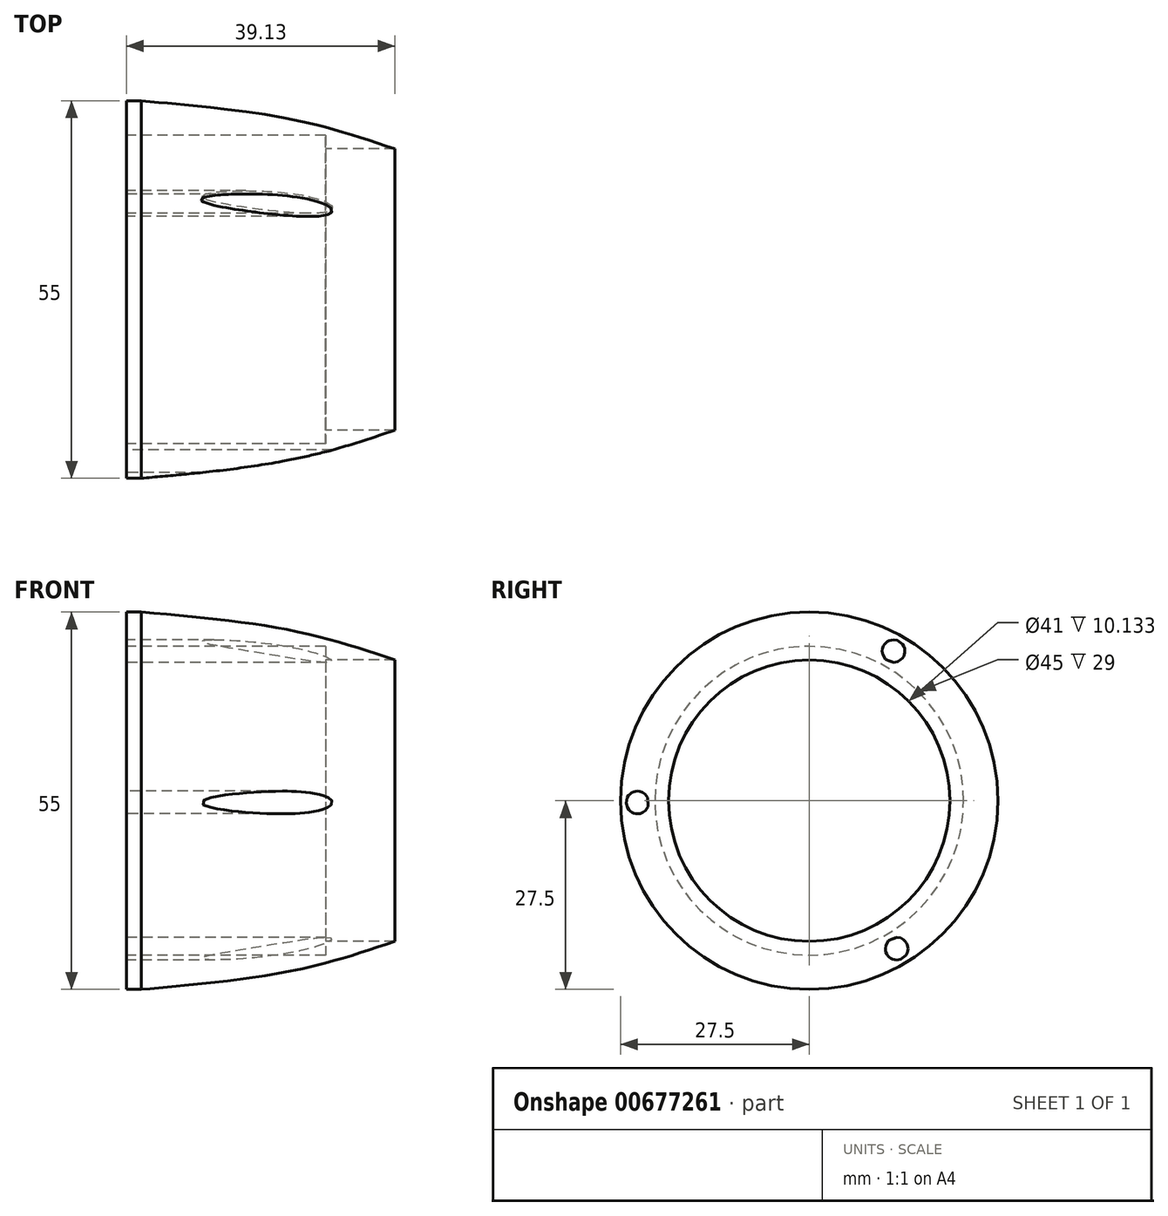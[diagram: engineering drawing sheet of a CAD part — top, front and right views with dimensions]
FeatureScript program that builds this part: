
annotation { "Feature Type Name" : "Feature", "Feature Type Description" : "" }
export const myFeature = defineFeature(function(context is Context, id is Id, definition is map)
    precondition{}
    {
        {
            var Q0;
            Q0=qCreatedBy(makeId("Front.planeOp"),FACE);
            var sketch = newSketch(context, id + "F0", { "sketchPlane" : qUnion([Q0])});
            skLineSegment(sketch, "E0", {"start": v(-29.3, 0) * mm, "end": v(30.63, 0) * mm, "construction": true});
            skLineSegment(sketch, "E1.top", {"start": v(-17.31, 22.5) * mm, "end": v(11.69, 22.5) * mm});
            skLineSegment(sketch, "E1.left", {"start": v(-17.31, 27.5) * mm, "end": v(-17.31, 22.5) * mm});
            skPoint(sketch, "E2", {"position": v(21.82, 20.5) * mm});
            skLineSegment(sketch, "E3", {"start": v(21.82, 20.5) * mm, "end": v(11.69, 20.5) * mm});
            skLineSegment(sketch, "E4", {"start": v(11.69, 20.5) * mm, "end": v(11.69, 22.5) * mm});
            skLineSegment(sketch, "E5", {"start": v(-17.31, 27.5) * mm, "end": v(-15.14, 27.5) * mm});
            skFitSpline(sketch, "E6", {"points": [v(-15.14, 27.5) * mm, v(6.94, 24.78) * mm, v(21.82, 20.5) * mm], "startDerivative": vector(42.6, -3.8) * mm, "endDerivative": vector(30.96, -10.4) * mm});
            skSolve(sketch);
        }
        {
            var Q0;
            Q0=makeQuery(id+"F0.imprint","IMPRINT",FACE,{"disambiguationData":[TD([[makeQuery(id+"F0.imprint","IMPRINT",EDGE,{"derivedFrom":sQuery(id+"F0.wireOp",EDGE,"E1.top")}),1.0]])]});
            var Q1;
            Q1=sQuery(id+"F0.wireOp",EDGE,"E0");
            revolve(context, id + "F1", {"entities" : qUnion([Q0]), "axis" : qUnion([Q1]), "revolveType" : RevolveType.FULL});
        }
        {
            var Q0;
            Q0=makeQuery(id+"F1.opRevolve","SWEPT_FACE",FACE,{"disambiguationData":[OSD([sQuery(id+"F0.wireOp",EDGE,"E1.left")])]});
            var sketch = newSketch(context, id + "F2", { "sketchPlane" : qUnion([Q0])});
            skCircle(sketch, "E7", {"center": v(-12.3, 21.8) * mm, "radius": 1.65 * mm});
            skCircle(sketch, "E8.1.0", {"center": v(-12.74, -21.55) * mm, "radius": 1.65 * mm});
            skCircle(sketch, "E8.2.0", {"center": v(25.03, -0.26) * mm, "radius": 1.65 * mm});
            skPoint(sketch, "E8.center", {"position": v(0, 0) * mm});
            skSolve(sketch);
        }
        {
            var Q0;
            Q0 = qSketchRegion(id + "F2", true);
            extrude(context, id + "F3", {"entities" : qUnion([Q0]), "operationType" : NewBodyOperationType.REMOVE, "oppositeDirection" : true, "depth" : 40 * mm, "offsetDistance" : 25 * mm});
        }
    });
